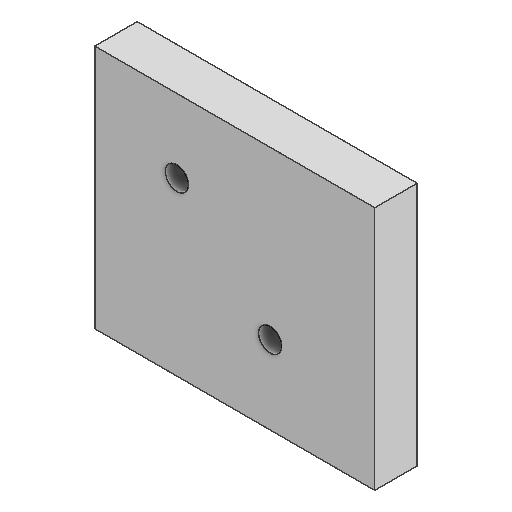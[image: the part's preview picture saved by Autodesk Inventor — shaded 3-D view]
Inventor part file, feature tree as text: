
AUTODESK INVENTOR PART (.ipt)
format: ipt  version: 2025 (Build 290162000, 162)  size: 95,744 bytes
history: native  units: mm
features: extrude x1, sketch x1
ambient origin geometry x8: Origin, YZ Plane, XZ Plane, XY Plane, X Axis, Y Axis, Z Axis, Center Point
bodies: Solid1 (feature_tree)
feature tree (2):
  extrude  "Extrusion1"  Depth=10.0mm
  sketch  "Sketch1"  dims[d0=5.5mm d1=5.5mm d2=22.0mm d3=22.0mm d4=22.0mm d5=10.0mm d6=0.0mm]
